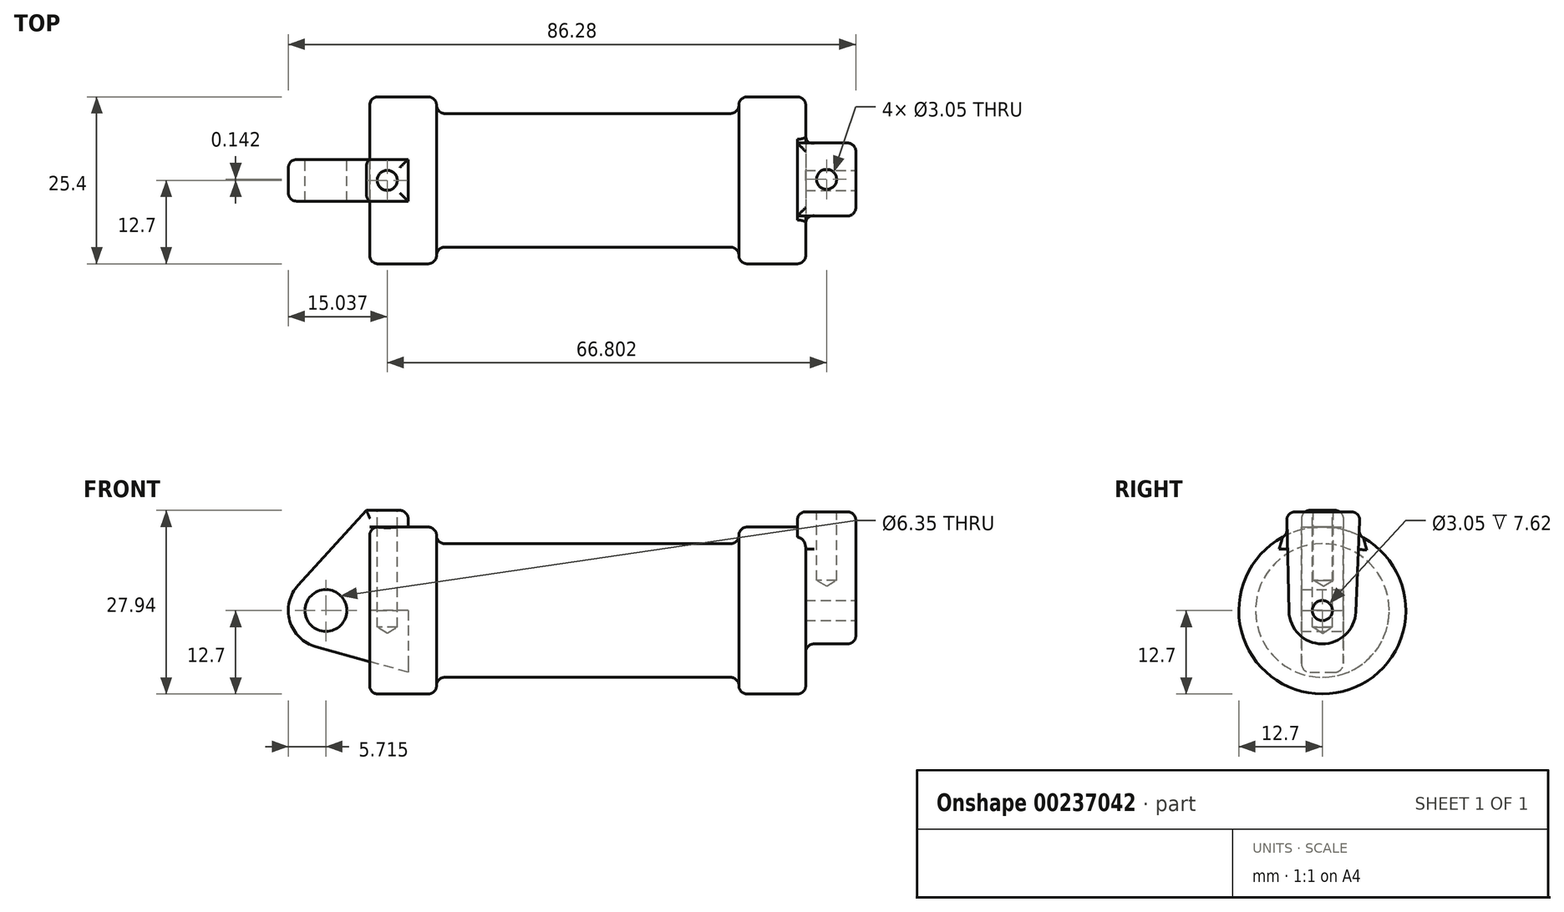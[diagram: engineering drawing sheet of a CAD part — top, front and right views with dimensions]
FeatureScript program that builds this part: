
annotation { "Feature Type Name" : "Feature", "Feature Type Description" : "" }
export const myFeature = defineFeature(function(context is Context, id is Id, definition is map)
    precondition{}
    {
        {
            var Q0;
            Q0=qCreatedBy(makeId("Front.planeOp"),FACE);
            var sketch = newSketch(context, id + "F0", { "sketchPlane" : qUnion([Q0])});
            skLineSegment(sketch, "E0", {"start": v(0, 0) * mm, "end": v(0, 12.7) * mm});
            skLineSegment(sketch, "E1", {"start": v(0, 12.7) * mm, "end": v(10.16, 12.7) * mm});
            skLineSegment(sketch, "E2", {"start": v(10.16, 12.7) * mm, "end": v(10.16, 10.16) * mm});
            skLineSegment(sketch, "E3", {"start": v(10.16, 10.16) * mm, "end": v(56.13, 10.16) * mm});
            skLineSegment(sketch, "E4", {"start": v(56.13, 10.16) * mm, "end": v(56.13, 12.7) * mm});
            skLineSegment(sketch, "E5", {"start": v(56.13, 12.7) * mm, "end": v(66.3, 12.7) * mm});
            skLineSegment(sketch, "E6", {"start": v(66.3, 12.7) * mm, "end": v(66.3, 0) * mm});
            skLineSegment(sketch, "E7", {"start": v(66.3, 0) * mm, "end": v(0, 0) * mm});
            skLineSegment(sketch, "E8", {"start": v(5.84, 15.24) * mm, "end": v(-0.5, 15.24) * mm});
            skLineSegment(sketch, "E9", {"start": v(-0.5, 15.24) * mm, "end": v(-10.88, 3.85) * mm});
            skLineSegment(sketch, "E10", {"start": v(0, 0) * mm, "end": v(-6.65, 0) * mm});
            skCircle(sketch, "E11", {"center": v(-6.65, 0) * mm, "radius": 5.72 * mm});
            skCircle(sketch, "E12", {"center": v(-6.65, 0) * mm, "radius": 3.18 * mm});
            skLineSegment(sketch, "E13", {"start": v(5.84, 15.24) * mm, "end": v(5.84, -9.4) * mm});
            skLineSegment(sketch, "E14", {"start": v(5.84, -9.4) * mm, "end": v(-8.18, -5.5) * mm});
            skSolve(sketch);
        }
        {
            var Q0;
            {var subQ0=sQuery(id+"F0.wireOp",EDGE,"E0");Q0=makeQuery(id+"F0.imprint","IMPRINT",FACE,{"disambiguationData":[TD([[makeQuery(id+"F0.imprint","IMPRINT",EDGE,{"derivedFrom":subQ0}),-1.0]])]});}
            var Q1;
            {var subQ0=sQuery(id+"F0.wireOp",EDGE,"E2");Q1=makeQuery(id+"F0.imprint","IMPRINT",FACE,{"disambiguationData":[TD([[makeQuery(id+"F0.imprint","IMPRINT",EDGE,{"derivedFrom":subQ0}),-1.0]])]});}
            var Q2;
            Q2=sQuery(id+"F0.wireOp",EDGE,"E7");
            revolve(context, id + "F1", {"entities" : qUnion([Q0, Q1]), "axis" : qUnion([Q2]), "revolveType" : RevolveType.FULL});
        }
        {
            var Q0;
            {var subQ3=sQuery(id+"F0.wireOp",EDGE,"E0");Q0=makeQuery(id+"F0.imprint","IMPRINT",FACE,{"disambiguationData":[TD([[makeQuery(id+"F0.imprint","IMPRINT",EDGE,{"derivedFrom":subQ3}),1.0]])]});}
            var Q1;
            {var subQ4=sQuery(id+"F0.wireOp",EDGE,"E12");Q1=makeQuery(id+"F0.imprint","IMPRINT",FACE,{"disambiguationData":[TD([[makeQuery(id+"F0.imprint","IMPRINT",EDGE,{"derivedFrom":subQ4}),-1.0]])]});}
            var Q2;
            {var subQ0=sQuery(id+"F0.wireOp",EDGE,"E14");Q2=makeQuery(id+"F0.imprint","IMPRINT",FACE,{"disambiguationData":[TD([[makeQuery(id+"F0.imprint","IMPRINT",EDGE,{"derivedFrom":subQ0}),-1.0]])]});}
            extrude(context, id + "F2", {"entities" : qUnion([Q0, Q1, Q2]), "endBound" : BoundingType.SYMMETRIC, "depth" : 6.35 * mm});
        }
        {
            var Q0;
            Q0=makeQuery(id+"F1.opRevolve","SWEPT_FACE",FACE,{"disambiguationData":[OSD([sQuery(id+"F0.wireOp",EDGE,"E6")])]});
            var sketch = newSketch(context, id + "F3", { "sketchPlane" : qUnion([Q0])});
            skCircle(sketch, "E15", {"center": v(0, 0) * mm, "radius": 1.52 * mm});
            skCircle(sketch, "E16", {"center": v(0, 0) * mm, "radius": 5.08 * mm});
            skLineSegment(sketch, "E17", {"start": v(-5.45, 15.02) * mm, "end": v(5.73, 15.02) * mm});
            skLineSegment(sketch, "E18", {"start": v(-5.45, 15.02) * mm, "end": v(-5.08, -0.12) * mm});
            skLineSegment(sketch, "E19", {"start": v(5.73, 15.02) * mm, "end": v(5.08, -0.22) * mm});
            skSolve(sketch);
        }
        {
            var Q0;
            {var subQ0=sQuery(id+"F3.wireOp",EDGE,"E17");Q0=makeQuery(id+"F3.imprint","IMPRINT",FACE,{"disambiguationData":[TD([[makeQuery(id+"F3.imprint","IMPRINT",EDGE,{"derivedFrom":subQ0}),-1.0]])]});}
            var Q1;
            {var subQ0=sQuery(id+"F3.wireOp",EDGE,"E18");var subQ1=sQuery(id+"F3.wireOp",EDGE,"E16");var subQ2=makeQuery(id+"F3.imprint","INTERSECT",VERTEX,{"derivedFrom":[subQ1,subQ0]});Q1=makeQuery(id+"F3.imprint","IMPRINT",FACE,{"disambiguationData":[TD([[makeQuery(id+"F3.imprint","IMPRINT",EDGE,{"disambiguationData":[TD([[subQ2,1.0]])],"derivedFrom":subQ1}),-1.0]])]});}
            var Q2;
            Q2=makeQuery(id+"F3.imprint","IMPRINT",FACE,{"disambiguationData":[TD([[makeQuery(id+"F3.imprint","IMPRINT",EDGE,{"derivedFrom":sQuery(id+"F3.wireOp",EDGE,"E15")}),-1.0]])]});
            extrude(context, id + "F4", {"entities" : qUnion([Q0, Q1, Q2]), "operationType" : NewBodyOperationType.ADD, "oppositeDirection" : true, "depth" : 1.27 * mm, "hasSecondDirection" : true, "secondDirectionOppositeDirection" : false, "secondDirectionDepth" : 7.62 * mm});
        }
        {
            var Q0;
            Q0=makeQuery(id+"F4.opExtrude","SWEPT_FACE",FACE,{"disambiguationData":[OSD([sQuery(id+"F3.wireOp",EDGE,"E17")])]});
            var sketch = newSketch(context, id + "F5", { "sketchPlane" : qUnion([Q0])});
            skCircle(sketch, "E20", {"center": v(69.47, 0.14) * mm, "radius": 1.52 * mm});
            skSolve(sketch);
        }
        {
            var Q0;
            Q0=sQuery(id+"F5.wireOp",VERTEX,"E20.center");
            var Q1;
            Q1=makeQuery(id+"F1.opRevolve","SWEPT_BODY",BODY,{"disambiguationData":[OSD([sQuery(id+"F0.wireOp",EDGE,"E0"),sQuery(id+"F0.wireOp",EDGE,"E1"),sQuery(id+"F0.wireOp",EDGE,"E2"),sQuery(id+"F0.wireOp",EDGE,"E3"),sQuery(id+"F0.wireOp",EDGE,"E4"),sQuery(id+"F0.wireOp",EDGE,"E5"),sQuery(id+"F0.wireOp",EDGE,"E6"),sQuery(id+"F0.wireOp",EDGE,"E7")])]});
            hole(context, id + "F6", {"style" : HoleStyle.SIMPLE, "endStyle" : HoleEndStyle.BLIND, "holeDiameter" : 3.05 * mm, "holeDepth" : 10.4 * mm, "locations" : qUnion([Q0]), "scope" : qUnion([Q1])});
        }
        {
            var Q0;
            Q0=makeQuery(id+"F2.opExtrude","SWEPT_FACE",FACE,{"disambiguationData":[OSD([sQuery(id+"F0.wireOp",EDGE,"E8")])]});
            var sketch = newSketch(context, id + "F7", { "sketchPlane" : qUnion([Q0])});
            skCircle(sketch, "E21", {"center": v(2.67, 0) * mm, "radius": 1.33 * mm});
            skSolve(sketch);
        }
        {
            var Q0;
            Q0=sQuery(id+"F7.wireOp",VERTEX,"E21.center");
            var Q1;
            Q1=makeQuery(id+"F1.opRevolve","SWEPT_BODY",BODY,{"disambiguationData":[OSD([sQuery(id+"F0.wireOp",EDGE,"E0"),sQuery(id+"F0.wireOp",EDGE,"E1"),sQuery(id+"F0.wireOp",EDGE,"E2"),sQuery(id+"F0.wireOp",EDGE,"E3"),sQuery(id+"F0.wireOp",EDGE,"E4"),sQuery(id+"F0.wireOp",EDGE,"E5"),sQuery(id+"F0.wireOp",EDGE,"E6"),sQuery(id+"F0.wireOp",EDGE,"E7")])]});
            var Q2;
            Q2=makeQuery(id+"F2.opExtrude","SWEPT_BODY",BODY,{"disambiguationData":[OSD([sQuery(id+"F0.wireOp",EDGE,"E0"),sQuery(id+"F0.wireOp",EDGE,"E1"),sQuery(id+"F0.wireOp",EDGE,"E7"),sQuery(id+"F0.wireOp",EDGE,"E8"),sQuery(id+"F0.wireOp",EDGE,"E9"),sQuery(id+"F0.wireOp",EDGE,"E11"),sQuery(id+"F0.wireOp",EDGE,"E12"),sQuery(id+"F0.wireOp",EDGE,"E13"),sQuery(id+"F0.wireOp",EDGE,"E14")])]});
            hole(context, id + "F8", {"style" : HoleStyle.SIMPLE, "endStyle" : HoleEndStyle.BLIND, "holeDiameter" : 3.05 * mm, "holeDepth" : 17.78 * mm, "locations" : qUnion([Q0]), "scope" : qUnion([Q1, Q2])});
        }
        {
            var Q0;
            Q0=makeQuery(id+"F1.opRevolve","SWEPT_EDGE",EDGE,{"disambiguationData":[OSD([sQuery(id+"F0.wireOp",EDGE,"E2"),sQuery(id+"F0.wireOp",EDGE,"E3")])]});
            var Q1;
            Q1=makeQuery(id+"F1.opRevolve","SWEPT_FACE",FACE,{"disambiguationData":[OSD([sQuery(id+"F0.wireOp",EDGE,"E3")])]});
            var Q2;
            Q2=makeQuery(id+"F1.opRevolve","SWEPT_EDGE",EDGE,{"disambiguationData":[OSD([sQuery(id+"F0.wireOp",EDGE,"E0"),sQuery(id+"F0.wireOp",EDGE,"E1")])]});
            var Q3;
            Q3=makeQuery(id+"F1.opRevolve","SWEPT_EDGE",EDGE,{"disambiguationData":[OSD([sQuery(id+"F0.wireOp",EDGE,"E5"),sQuery(id+"F0.wireOp",EDGE,"E6")])]});
            var Q4;
            Q4=makeQuery(id+"F1.opRevolve","SWEPT_EDGE",EDGE,{"disambiguationData":[OSD([sQuery(id+"F0.wireOp",EDGE,"E4"),sQuery(id+"F0.wireOp",EDGE,"E5")])]});
            var Q5;
            Q5=makeQuery(id+"F1.opRevolve","SWEPT_EDGE",EDGE,{"disambiguationData":[OSD([sQuery(id+"F0.wireOp",EDGE,"E1"),sQuery(id+"F0.wireOp",EDGE,"E2")])]});
            fillet(context, id + "F9", {"entities" : qUnion([Q0, Q1, Q2, Q3, Q4, Q5]), "radius" : 1.27 * mm, "tangentPropagation" : true, "allowEdgeOverflow" : false});
        }
        {
            var Q0;
            Q0=makeQuery(id+"F2.opExtrude","CAP_EDGE",EDGE,{"disambiguationData":[OSD([sQuery(id+"F0.wireOp",EDGE,"E8")])],"isStart":true});
            var Q1;
            Q1=makeQuery(id+"F2.opExtrude","CAP_EDGE",EDGE,{"disambiguationData":[OSD([sQuery(id+"F0.wireOp",EDGE,"E8")])],"isStart":false});
            var Q2;
            Q2=makeQuery(id+"F2.opExtrude","SWEPT_EDGE",EDGE,{"disambiguationData":[OSD([sQuery(id+"F0.wireOp",EDGE,"E8"),sQuery(id+"F0.wireOp",EDGE,"E13")])]});
            var Q3;
            Q3=makeQuery(id+"F2.opExtrude","CAP_EDGE",EDGE,{"disambiguationData":[OSD([sQuery(id+"F0.wireOp",EDGE,"E9")])],"isStart":true});
            var Q4;
            Q4=makeQuery(id+"F2.opExtrude","CAP_EDGE",EDGE,{"disambiguationData":[OSD([sQuery(id+"F0.wireOp",EDGE,"E9")])],"isStart":false});
            var Q5;
            Q5=makeQuery(id+"F2.opExtrude","CAP_EDGE",EDGE,{"disambiguationData":[OSD([sQuery(id+"F0.wireOp",EDGE,"E11")])],"isStart":false});
            var Q6;
            Q6=makeQuery(id+"F2.opExtrude","CAP_EDGE",EDGE,{"disambiguationData":[OSD([sQuery(id+"F0.wireOp",EDGE,"E11")])],"isStart":true});
            fillet(context, id + "F10", {"entities" : qUnion([Q0, Q1, Q2, Q3, Q4, Q5, Q6]), "radius" : 1.27 * mm, "tangentPropagation" : true, "allowEdgeOverflow" : false});
        }
        {
            var Q0;
            Q0=makeQuery(id+"F4.opExtrude","SWEPT_EDGE",EDGE,{"disambiguationData":[OSD([sQuery(id+"F3.wireOp",EDGE,"E17"),sQuery(id+"F3.wireOp",EDGE,"E18")])]});
            var Q1;
            Q1=makeQuery(id+"F4.opExtrude","CAP_EDGE",EDGE,{"disambiguationData":[OSD([sQuery(id+"F3.wireOp",EDGE,"E17")])],"isStart":true});
            var Q2;
            Q2=makeQuery(id+"F4.opExtrude","SWEPT_EDGE",EDGE,{"disambiguationData":[OSD([sQuery(id+"F3.wireOp",EDGE,"E17"),sQuery(id+"F3.wireOp",EDGE,"E19")])]});
            var Q3;
            Q3=makeQuery(id+"F4.opExtrude","CAP_EDGE",EDGE,{"disambiguationData":[OSD([sQuery(id+"F3.wireOp",EDGE,"E17")])],"isStart":false});
            var Q4;
            Q4=makeQuery(id+"F4.opExtrude","CAP_EDGE",EDGE,{"disambiguationData":[OSD([sQuery(id+"F3.wireOp",EDGE,"E18")])],"isStart":true});
            var Q5;
            Q5=makeQuery(id+"F4.opExtrude","SWEPT_FACE",FACE,{"disambiguationData":[OSD([sQuery(id+"F3.wireOp",EDGE,"E16")])]});
            var Q6;
            Q6=makeQuery(id+"F4.opExtrude","CAP_EDGE",EDGE,{"disambiguationData":[OSD([sQuery(id+"F3.wireOp",EDGE,"E19")])],"isStart":true});
            var Q7;
            Q7=makeQuery(id+"F4.boolean.opBoolean","INTERSECT",EDGE,{"derivedFrom":[makeQuery(id+"F1.opRevolve","SWEPT_FACE",FACE,{"disambiguationData":[OSD([sQuery(id+"F0.wireOp",EDGE,"E6")])]}),makeQuery(id+"F4.opExtrude","SWEPT_FACE",FACE,{"disambiguationData":[OSD([sQuery(id+"F3.wireOp",EDGE,"E19")])]})]});
            var Q8;
            Q8=makeQuery(id+"F4.boolean.opBoolean","INTERSECT",EDGE,{"derivedFrom":[makeQuery(id+"F1.opRevolve","SWEPT_FACE",FACE,{"disambiguationData":[OSD([sQuery(id+"F0.wireOp",EDGE,"E6")])]}),makeQuery(id+"F4.opExtrude","SWEPT_FACE",FACE,{"disambiguationData":[OSD([sQuery(id+"F3.wireOp",EDGE,"E18")])]})]});
            var Q9;
            Q9=makeQuery(id+"F9.opFillet","BLEND_EDGE",EDGE,{"blendedFrom":[makeQuery(id+"F1.opRevolve","SWEPT_EDGE",EDGE,{"disambiguationData":[OSD([sQuery(id+"F0.wireOp",EDGE,"E5"),sQuery(id+"F0.wireOp",EDGE,"E6")])]}),makeQuery(id+"F4.opExtrude","SWEPT_FACE",FACE,{"disambiguationData":[OSD([sQuery(id+"F3.wireOp",EDGE,"E18")])]})],"blendedInto":[makeQuery(id+"F4.opExtrude","SWEPT_FACE",FACE,{"disambiguationData":[OSD([sQuery(id+"F3.wireOp",EDGE,"E18")])]})]});
            var Q10;
            Q10=makeQuery(id+"F9.opFillet","BLEND_EDGE",EDGE,{"blendedFrom":[makeQuery(id+"F1.opRevolve","SWEPT_EDGE",EDGE,{"disambiguationData":[OSD([sQuery(id+"F0.wireOp",EDGE,"E5"),sQuery(id+"F0.wireOp",EDGE,"E6")])]}),makeQuery(id+"F4.opExtrude","SWEPT_FACE",FACE,{"disambiguationData":[OSD([sQuery(id+"F3.wireOp",EDGE,"E19")])]})],"blendedInto":[makeQuery(id+"F4.opExtrude","SWEPT_FACE",FACE,{"disambiguationData":[OSD([sQuery(id+"F3.wireOp",EDGE,"E19")])]})]});
            fillet(context, id + "F11", {"entities" : qUnion([Q0, Q1, Q2, Q3, Q4, Q5, Q6, Q7, Q8, Q9, Q10]), "radius" : 1.27 * mm, "tangentPropagation" : true, "allowEdgeOverflow" : false});
        }
    });
